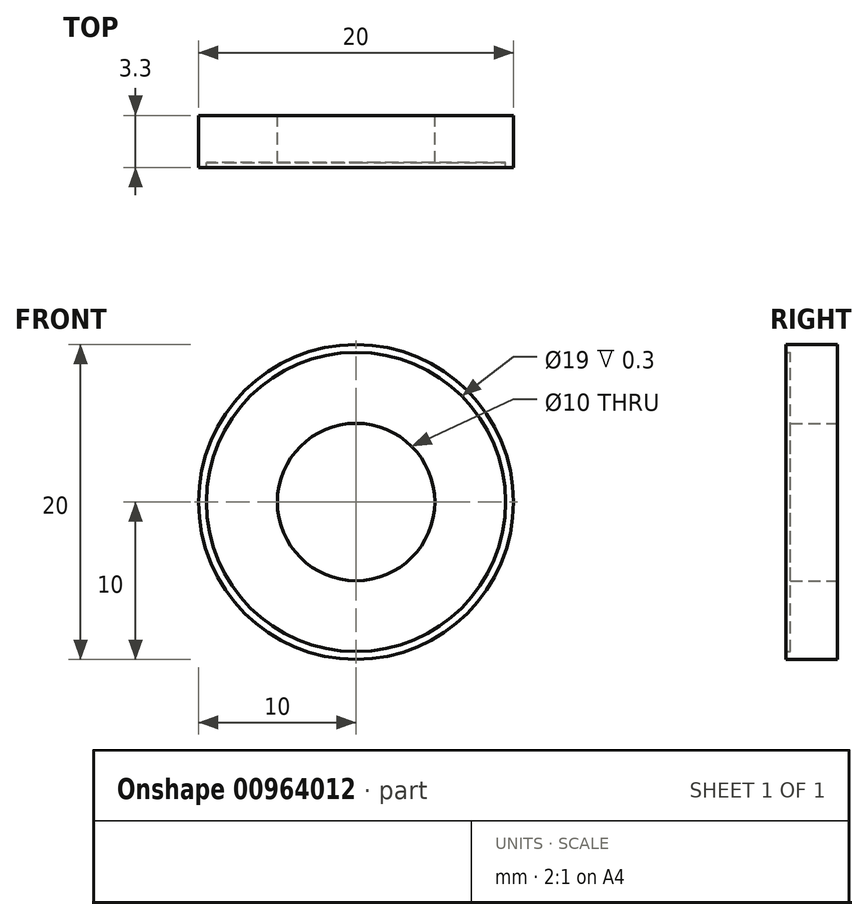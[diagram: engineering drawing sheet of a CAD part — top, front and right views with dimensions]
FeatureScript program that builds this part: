
annotation { "Feature Type Name" : "Feature", "Feature Type Description" : "" }
export const myFeature = defineFeature(function(context is Context, id is Id, definition is map)
    precondition{}
    {
        {
            var Q0;
            Q0=qCreatedBy(makeId("Front.planeOp"),FACE);
            var sketch = newSketch(context, id + "F0", { "sketchPlane" : qUnion([Q0])});
            skCircle(sketch, "E0", {"center": v(0, 0) * mm, "radius": 10 * mm});
            skCircle(sketch, "E1", {"center": v(0, 0) * mm, "radius": 5 * mm});
            skCircle(sketch, "E2", {"center": v(0, 0) * mm, "radius": 9.5 * mm});
            skSolve(sketch);
        }
        {
            var Q0;
            Q0=makeQuery(id+"F0.imprint","IMPRINT",FACE,{"disambiguationData":[TD([[makeQuery(id+"F0.imprint","IMPRINT",EDGE,{"derivedFrom":sQuery(id+"F0.wireOp",EDGE,"E0")}),1.0]])]});
            extrude(context, id + "F1", {"entities" : qUnion([Q0]), "depth" : 3.3 * mm, "offsetDistance" : 25 * mm});
        }
        {
            var Q0;
            Q0=makeQuery(id+"F0.imprint","IMPRINT",FACE,{"disambiguationData":[TD([[makeQuery(id+"F0.imprint","IMPRINT",EDGE,{"derivedFrom":sQuery(id+"F0.wireOp",EDGE,"E1")}),-1.0]])]});
            var Q1;
            Q1=makeQuery(id+"F0.imprint","IMPRINT",FACE,{"disambiguationData":[TD([[makeQuery(id+"F0.imprint","IMPRINT",EDGE,{"derivedFrom":sQuery(id+"F0.wireOp",EDGE,"E1")}),1.0]])]});
            extrude(context, id + "F2", {"entities" : qUnion([Q0, Q1]), "operationType" : NewBodyOperationType.ADD, "depth" : 3 * mm, "offsetDistance" : 25 * mm});
        }
        {
            var Q0;
            Q0=makeQuery(id+"F0.imprint","IMPRINT",FACE,{"disambiguationData":[TD([[makeQuery(id+"F0.imprint","IMPRINT",EDGE,{"derivedFrom":sQuery(id+"F0.wireOp",EDGE,"E1")}),1.0]])]});
            extrude(context, id + "F3", {"entities" : qUnion([Q0]), "operationType" : NewBodyOperationType.REMOVE, "depth" : 25 * mm, "offsetDistance" : 25 * mm});
        }
    });
